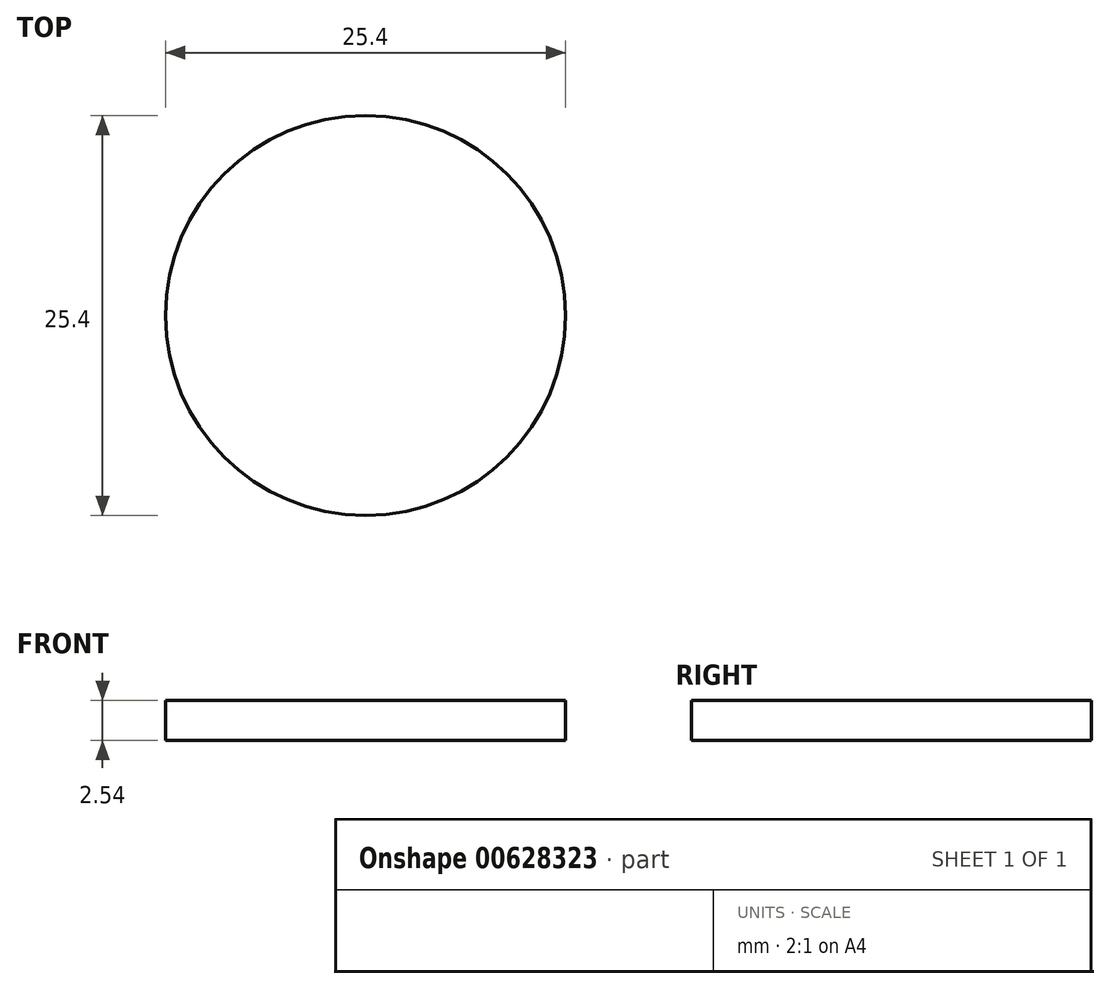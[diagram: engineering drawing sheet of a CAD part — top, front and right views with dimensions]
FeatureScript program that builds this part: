
annotation { "Feature Type Name" : "Feature", "Feature Type Description" : "" }
export const myFeature = defineFeature(function(context is Context, id is Id, definition is map)
    precondition{}
    {
        {
            var Q0;
            Q0=qCreatedBy(makeId("Top.planeOp"),FACE);
            var sketch = newSketch(context, id + "F0", { "sketchPlane" : qUnion([Q0])});
            skCircle(sketch, "E0", {"center": v(0, 0) * mm, "radius": 12.7 * mm});
            skSolve(sketch);
        }
        {
            var Q0;
            Q0=makeQuery(id+"F0.imprint","IMPRINT",FACE,{"disambiguationData":[TD([[makeQuery(id+"F0.imprint","IMPRINT",EDGE,{"derivedFrom":sQuery(id+"F0.wireOp",EDGE,"E0")}),1.0]])]});
            extrude(context, id + "F1", {"entities" : qUnion([Q0]), "depth" : 2.54 * mm, "offsetDistance" : 25.4 * mm});
        }
    });
